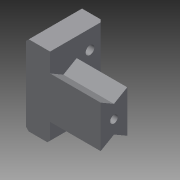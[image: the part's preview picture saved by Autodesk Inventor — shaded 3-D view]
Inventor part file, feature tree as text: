
AUTODESK INVENTOR PART (.ipt)
format: ipt  version: 2015 (Build 190159000, 159)  size: 160,256 bytes
history: native  units: mm
features: other x4, extrude x4, sketch x4, hole x3, chamfer x2, projected_geometry x1
ambient origin geometry x8: Origin, YZ Plane, XZ Plane, XY Plane, X Axis, Y Axis, Z Axis, Center Point
bodies: Body1 (feature_tree)
feature tree (18):
  other  "솔리드1"
  extrude  "돌출1"  Depth=9.0mm
  extrude  "돌출2"  Depth=30.0mm
  hole  "구멍1"  [1 undecoded]
  hole  "구멍2"  [1 undecoded]
  extrude  "돌출5"  Depth=16.0mm TaperAngle=0.0deg
  extrude  "돌출6"  Depth=3.0mm TaperAngle=0.0deg
  hole  "구멍4"  [1 undecoded]
  other  "두껍게 하기1"
  other  "두껍게 하기2"
  other  "두껍게 하기3"
  chamfer  "모따기1"  Distance=0.2mm
  chamfer  "모따기2"  Distance=6.0mm
  sketch  "스케치1"
  sketch  "스케치2"
  sketch  "스케치5"
  sketch  "스케치6"
  projected_geometry  "투영된 루프2"
note: 3 required parameter values undecoded (feature->parameter linkage not recoverable at this tier; creation-order binding heuristic only, values carry confidence <= 0.55)
